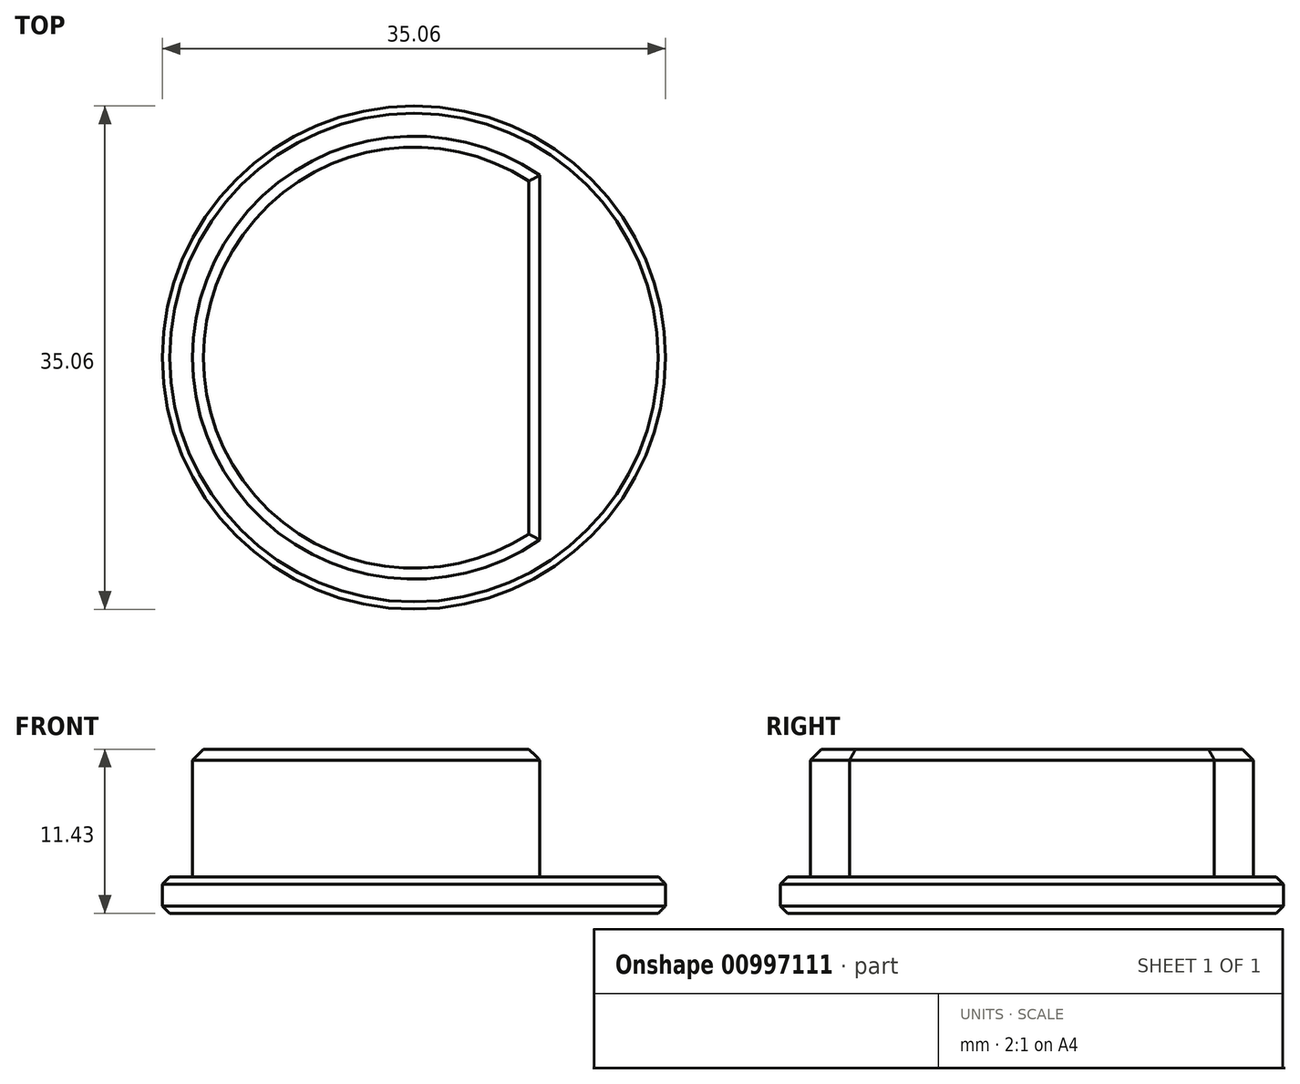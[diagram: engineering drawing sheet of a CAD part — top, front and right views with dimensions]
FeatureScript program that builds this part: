
annotation { "Feature Type Name" : "Feature", "Feature Type Description" : "" }
export const myFeature = defineFeature(function(context is Context, id is Id, definition is map)
    precondition{}
    {
        {
            var Q0;
            Q0=qCreatedBy(makeId("Top.planeOp"),FACE);
            var sketch = newSketch(context, id + "F0", { "sketchPlane" : qUnion([Q0])});
            skCircle(sketch, "E0", {"center": v(0, 0) * mm, "radius": 17.53 * mm});
            skSolve(sketch);
        }
        {
            var Q0;
            Q0=makeQuery(id+"F0.imprint","IMPRINT",FACE,{"disambiguationData":[TD([[makeQuery(id+"F0.imprint","IMPRINT",EDGE,{"derivedFrom":sQuery(id+"F0.wireOp",EDGE,"E0")}),1.0]])]});
            extrude(context, id + "F1", {"entities" : qUnion([Q0]), "depth" : 2.54 * mm, "offsetDistance" : 25.4 * mm});
        }
        {
            var Q0;
            Q0=makeQuery(id+"F1.opExtrude","CAP_FACE",FACE,{"disambiguationData":[OSD([sQuery(id+"F0.wireOp",EDGE,"E0")])],"isStart":false});
            var sketch = newSketch(context, id + "F2", { "sketchPlane" : qUnion([Q0])});
            skArc(sketch, "E1", {"start": v(8.76, 12.7) * mm, "mid": v(-15.43, 0) * mm, "end": v(8.76, -12.7) * mm});
            skLineSegment(sketch, "E2", {"start": v(8.76, 12.7) * mm, "end": v(8.76, -12.7) * mm});
            skSolve(sketch);
        }
        {
            var Q0;
            Q0 = qSketchRegion(id + "F2", true);
            extrude(context, id + "F3", {"entities" : qUnion([Q0]), "operationType" : NewBodyOperationType.ADD, "depth" : 8.9 * mm, "offsetDistance" : 25.4 * mm});
        }
        {
            var Q0;
            Q0=makeQuery(id+"F3.opExtrude","CAP_EDGE",EDGE,{"disambiguationData":[OSD([sQuery(id+"F2.wireOp",EDGE,"E1")])],"isStart":false});
            var Q1;
            Q1=makeQuery(id+"F3.opExtrude","CAP_EDGE",EDGE,{"disambiguationData":[OSD([sQuery(id+"F2.wireOp",EDGE,"E2")])],"isStart":false});
            var Q2;
            Q2=makeQuery(id+"F3.opExtrude","CAP_EDGE",EDGE,{"disambiguationData":[OSD([sQuery(id+"F2.wireOp",EDGE,"E2")])],"isStart":true});
            var Q3;
            Q3=makeQuery(id+"F3.opExtrude","CAP_EDGE",EDGE,{"disambiguationData":[OSD([sQuery(id+"F2.wireOp",EDGE,"E1")])],"isStart":true});
            chamfer(context, id + "F4", {"entities" : qUnion([Q0, Q1, Q2, Q3]), "width" : 0.76 * mm, "tangentPropagation" : true});
        }
        {
            var Q0;
            Q0=makeQuery(id+"F1.opExtrude","CAP_EDGE",EDGE,{"disambiguationData":[OSD([sQuery(id+"F0.wireOp",EDGE,"E0")])],"isStart":false});
            var Q1;
            Q1=makeQuery(id+"F1.opExtrude","CAP_EDGE",EDGE,{"disambiguationData":[OSD([sQuery(id+"F0.wireOp",EDGE,"E0")])],"isStart":true});
            chamfer(context, id + "F5", {"entities" : qUnion([Q0, Q1]), "width" : 0.5 * mm, "tangentPropagation" : true});
        }
    });
